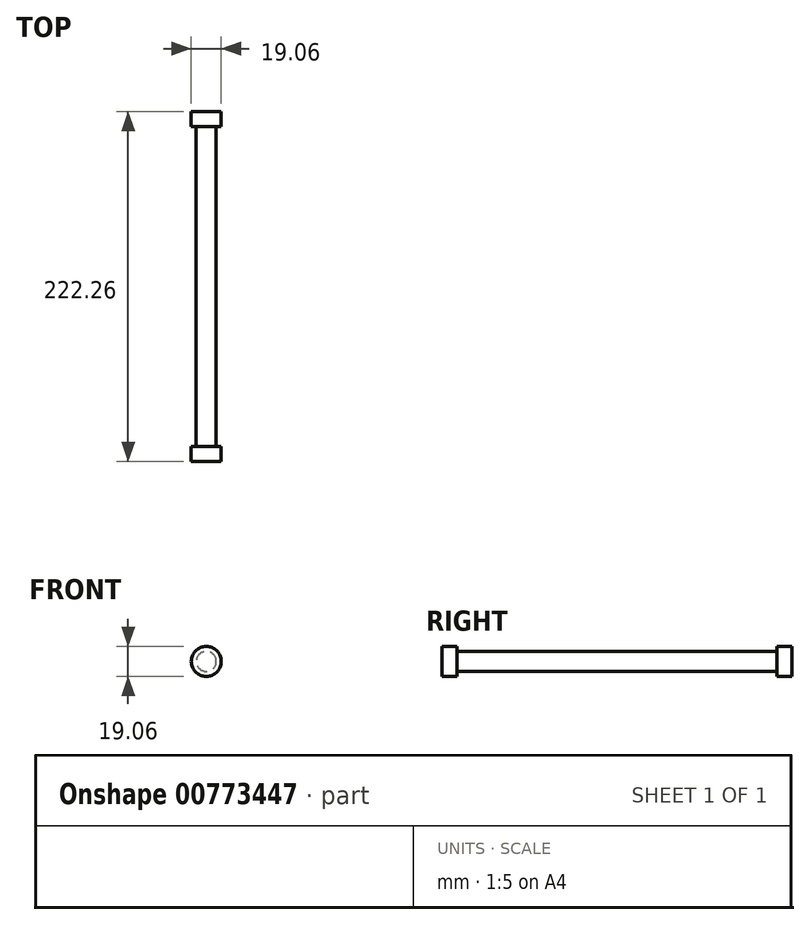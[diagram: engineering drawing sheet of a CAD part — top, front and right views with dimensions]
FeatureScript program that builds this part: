
annotation { "Feature Type Name" : "Feature", "Feature Type Description" : "" }
export const myFeature = defineFeature(function(context is Context, id is Id, definition is map)
    precondition{}
    {
        {
            var Q0;
            Q0=qCreatedBy(makeId("Front.planeOp"),FACE);
            var sketch = newSketch(context, id + "F0", { "sketchPlane" : qUnion([Q0])});
            skCircle(sketch, "E0", {"center": v(0, 0) * mm, "radius": 6.35 * mm});
            skSolve(sketch);
        }
        {
            var Q0;
            Q0 = qSketchRegion(id + "F0", true);
            extrude(context, id + "F1", {"entities" : qUnion([Q0]), "depth" : 203.2 * mm, "offsetDistance" : 25.4 * mm, "symmetric" : true});
        }
        {
            var Q0;
            Q0=makeQuery(id+"F1.opExtrude","CAP_FACE",FACE,{"disambiguationData":[OSD([sQuery(id+"F0.wireOp",EDGE,"E0")])],"isStart":false});
            var sketch = newSketch(context, id + "F2", { "sketchPlane" : qUnion([Q0])});
            skCircle(sketch, "E1", {"center": v(0, 0) * mm, "radius": 9.53 * mm});
            skSolve(sketch);
        }
        {
            var Q0;
            Q0 = qSketchRegion(id + "F2", true);
            extrude(context, id + "F3", {"entities" : qUnion([Q0]), "operationType" : NewBodyOperationType.ADD, "depth" : 9.52 * mm, "offsetDistance" : 25.4 * mm});
        }
        {
            var Q0;
            Q0=makeQuery(id+"F1.opExtrude","CAP_FACE",FACE,{"disambiguationData":[OSD([sQuery(id+"F0.wireOp",EDGE,"E0")])],"isStart":true});
            var sketch = newSketch(context, id + "F4", { "sketchPlane" : qUnion([Q0])});
            skCircle(sketch, "E2", {"center": v(0, 0) * mm, "radius": 9.53 * mm});
            skSolve(sketch);
        }
        {
            var Q0;
            Q0 = qSketchRegion(id + "F4", true);
            extrude(context, id + "F5", {"entities" : qUnion([Q0]), "operationType" : NewBodyOperationType.ADD, "depth" : 9.52 * mm, "offsetDistance" : 25.4 * mm});
        }
    });
